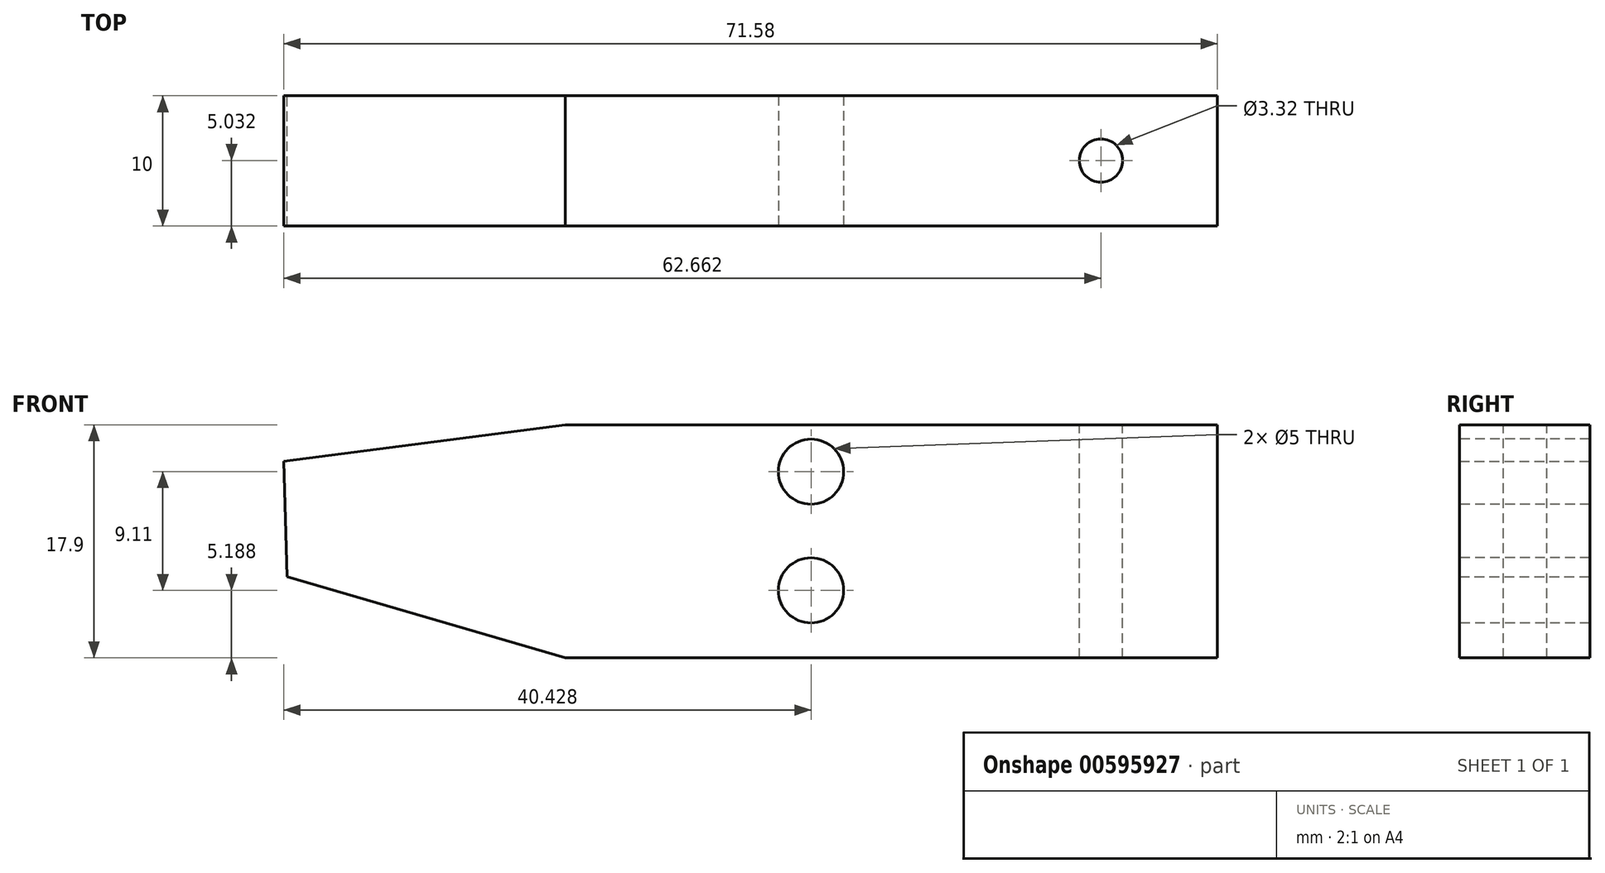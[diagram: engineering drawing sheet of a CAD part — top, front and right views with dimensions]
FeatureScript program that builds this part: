
annotation { "Feature Type Name" : "Feature", "Feature Type Description" : "" }
export const myFeature = defineFeature(function(context is Context, id is Id, definition is map)
    precondition{}
    {
        {
            var Q0;
            Q0=qCreatedBy(makeId("Front.planeOp"),FACE);
            var sketch = newSketch(context, id + "F0", { "sketchPlane" : qUnion([Q0])});
            skLineSegment(sketch, "E0.bottom", {"start": v(-11.59, 5.8) * mm, "end": v(13.41, 5.8) * mm});
            skLineSegment(sketch, "E0.top", {"start": v(-11.59, -12.1) * mm, "end": v(13.41, -12.1) * mm});
            skLineSegment(sketch, "E0.left", {"start": v(-11.59, 5.8) * mm, "end": v(-11.59, -12.1) * mm});
            skLineSegment(sketch, "E0.right", {"start": v(13.41, 5.8) * mm, "end": v(13.41, -12.1) * mm});
            skLineSegment(sketch, "E1", {"start": v(-11.59, 5.8) * mm, "end": v(-33.17, 3) * mm});
            skLineSegment(sketch, "E2", {"start": v(-11.59, -12.1) * mm, "end": v(-32.91, -5.88) * mm});
            skLineSegment(sketch, "E3", {"start": v(-33.17, 3) * mm, "end": v(-32.91, -5.88) * mm});
            skSolve(sketch);
        }
        {
            var Q0;
            Q0=makeQuery(id+"F0.imprint","IMPRINT",FACE,{"disambiguationData":[TD([[makeQuery(id+"F0.imprint","IMPRINT",EDGE,{"derivedFrom":sQuery(id+"F0.wireOp",EDGE,"E0.left")}),-1.0]])]});
            var Q1;
            Q1=makeQuery(id+"F0.imprint","IMPRINT",FACE,{"disambiguationData":[TD([[makeQuery(id+"F0.imprint","IMPRINT",EDGE,{"derivedFrom":sQuery(id+"F0.wireOp",EDGE,"E0.bottom")}),-1.0]])]});
            extrude(context, id + "F1", {"entities" : qUnion([Q0, Q1]), "depth" : 10 * mm, "offsetDistance" : 25 * mm});
        }
        {
            var Q0;
            Q0=makeQuery(id+"F1.opExtrude","CAP_FACE",FACE,{"disambiguationData":[OSD([sQuery(id+"F0.wireOp",EDGE,"E0.bottom"),sQuery(id+"F0.wireOp",EDGE,"E0.top"),sQuery(id+"F0.wireOp",EDGE,"E0.right"),sQuery(id+"F0.wireOp",EDGE,"E1"),sQuery(id+"F0.wireOp",EDGE,"E2"),sQuery(id+"F0.wireOp",EDGE,"E3")])],"isStart":false});
            var sketch = newSketch(context, id + "F2", { "sketchPlane" : qUnion([Q0])});
            skCircle(sketch, "E4", {"center": v(7.26, 2.19) * mm, "radius": 2.84 * mm});
            skCircle(sketch, "E5", {"center": v(7.26, -6.92) * mm, "radius": 2.84 * mm});
            skSolve(sketch);
        }
        {
            var Q0;
            Q0=sQuery(id+"F2.wireOp",VERTEX,"E4.center");
            var Q1;
            Q1=sQuery(id+"F2.wireOp",VERTEX,"uiojgvC1-7o9L-HfFJ-H1Jm-jQC7qf7ywTfV.center");
            var Q2;
            Q2=sQuery(id+"F2.wireOp",VERTEX,"E5.center");
            var Q3;
            Q3=makeQuery(id+"F1.opExtrude","SWEPT_BODY",BODY,{"disambiguationData":[OSD([sQuery(id+"F0.wireOp",EDGE,"E0.bottom"),sQuery(id+"F0.wireOp",EDGE,"E0.top"),sQuery(id+"F0.wireOp",EDGE,"E0.right"),sQuery(id+"F0.wireOp",EDGE,"E1"),sQuery(id+"F0.wireOp",EDGE,"E2"),sQuery(id+"F0.wireOp",EDGE,"E3")])]});
            hole(context, id + "F3", {"style" : HoleStyle.SIMPLE, "endStyle" : HoleEndStyle.THROUGH, "holeDiameter" : 5 * mm, "isTappedThrough" : true, "tappedDepth" : 12 * mm, "tapClearance" : 3, "locations" : qUnion([Q0, Q1, Q2]), "scope" : qUnion([Q3]), "majorDiameter" : 5 * mm});
        }
        {
            var Q0;
            Q0=makeQuery(id+"F1.opExtrude","SWEPT_FACE",FACE,{"disambiguationData":[OSD([sQuery(id+"F0.wireOp",EDGE,"E0.right")])]});
            var sketch = newSketch(context, id + "F4", { "sketchPlane" : qUnion([Q0])});
            skLineSegment(sketch, "E6.bottom", {"start": v(-10, 5.8) * mm, "end": v(0, 5.8) * mm});
            skLineSegment(sketch, "E6.top", {"start": v(-10, -12.1) * mm, "end": v(0, -12.1) * mm});
            skLineSegment(sketch, "E6.left", {"start": v(-10, 5.8) * mm, "end": v(-10, -12.1) * mm});
            skLineSegment(sketch, "E6.right", {"start": v(0, 5.8) * mm, "end": v(0, -12.1) * mm});
            skSolve(sketch);
        }
        {
            var Q0;
            Q0=qSketchRegion(id+"F4",true);
            extrude(context, id + "F5", {"entities" : qUnion([Q0]), "operationType" : NewBodyOperationType.ADD, "depth" : 25 * mm, "offsetDistance" : 25 * mm});
        }
        {
            var Q0;
            Q0=makeQuery(id+"F5.boolean.opBoolean","MERGE",FACE,{"derivedFrom":[makeQuery(id+"F1.opExtrude","SWEPT_FACE",FACE,{"disambiguationData":[OSD([sQuery(id+"F0.wireOp",EDGE,"E0.bottom")])]}),makeQuery(id+"F5.opExtrude","SWEPT_FACE",FACE,{"disambiguationData":[OSD([sQuery(id+"F4.wireOp",EDGE,"E6.bottom")])]})]});
            var sketch = newSketch(context, id + "F6", { "sketchPlane" : qUnion([Q0])});
            skCircle(sketch, "E7", {"center": v(29.5, -4.97) * mm, "radius": 1.66 * mm});
            skSolve(sketch);
        }
        {
            var Q0;
            Q0=qSketchRegion(id+"F6",true);
            extrude(context, id + "F7", {"entities" : qUnion([Q0]), "operationType" : NewBodyOperationType.REMOVE, "oppositeDirection" : true, "depth" : 25 * mm, "offsetDistance" : 25 * mm});
        }
    });
